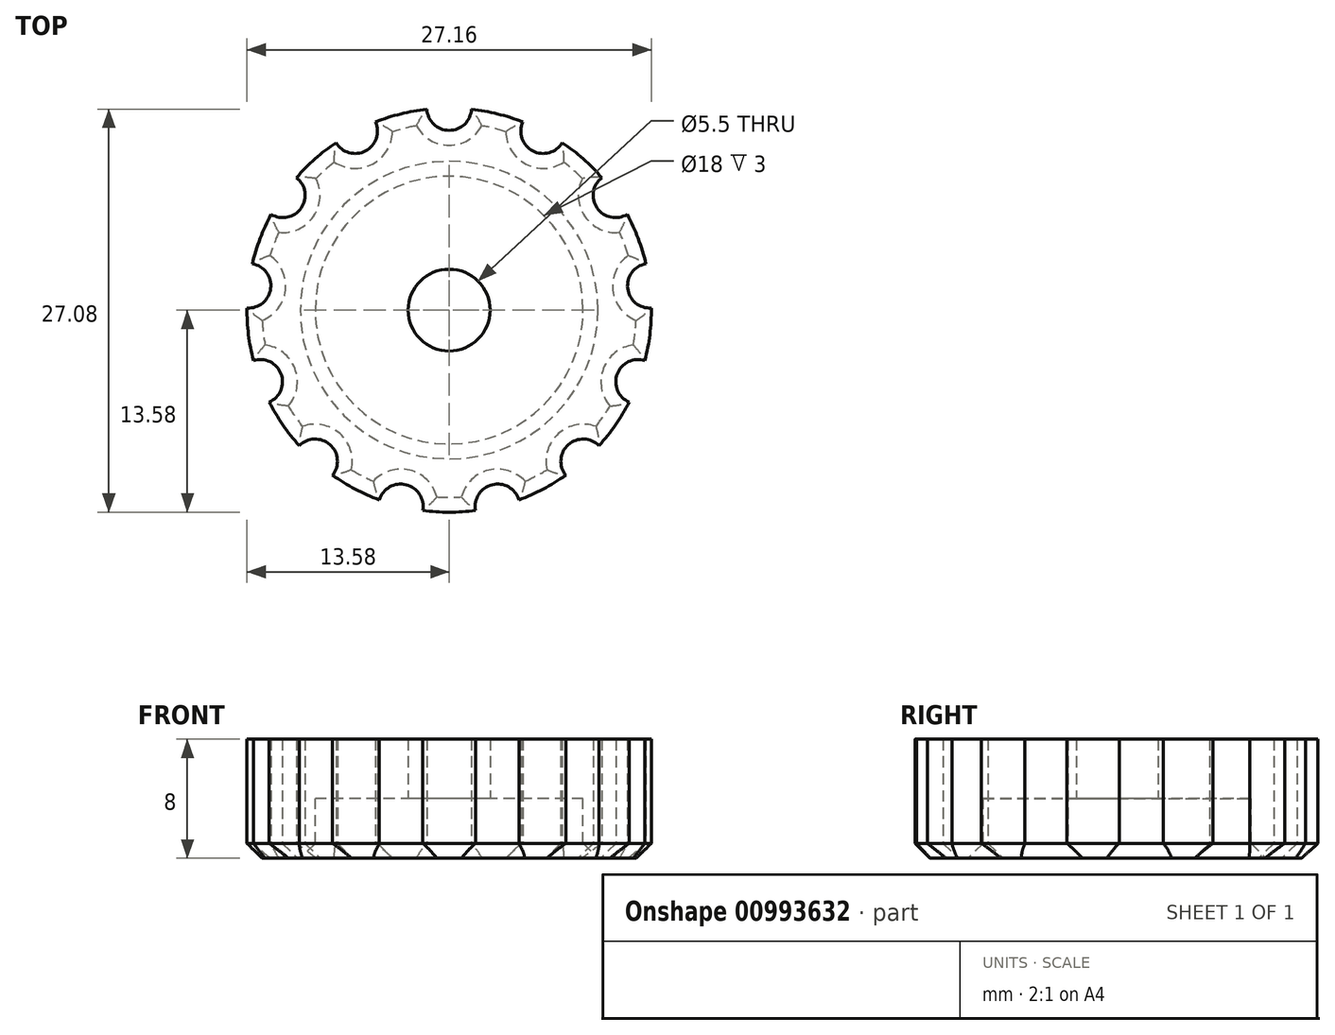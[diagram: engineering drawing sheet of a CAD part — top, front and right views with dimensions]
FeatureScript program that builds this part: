
annotation { "Feature Type Name" : "Feature", "Feature Type Description" : "" }
export const myFeature = defineFeature(function(context is Context, id is Id, definition is map)
    precondition{}
    {
        {
            var Q0;
            Q0=qCreatedBy(makeId("Top.planeOp"),FACE);
            var sketch = newSketch(context, id + "F0", { "sketchPlane" : qUnion([Q0])});
            skCircle(sketch, "E0", {"center": v(0, 0) * mm, "radius": 2.75 * mm});
            skCircle(sketch, "E1", {"center": v(0, 0) * mm, "radius": 13.58 * mm});
            skCircle(sketch, "E2", {"center": v(0, 13.58) * mm, "radius": 1.5 * mm});
            skCircle(sketch, "E3.1.0", {"center": v(-6.31, 12.02) * mm, "radius": 1.5 * mm});
            skCircle(sketch, "E3.2.0", {"center": v(-11.18, 7.71) * mm, "radius": 1.5 * mm});
            skCircle(sketch, "E3.3.0", {"center": v(-13.48, 1.64) * mm, "radius": 1.5 * mm});
            skCircle(sketch, "E3.4.0", {"center": v(-12.7, -4.82) * mm, "radius": 1.5 * mm});
            skCircle(sketch, "E3.5.0", {"center": v(-9, -10.16) * mm, "radius": 1.5 * mm});
            skPoint(sketch, "E4", {"position": v(1.5, 13.5) * mm});
            skPoint(sketch, "E5", {"position": v(4.95, 12.65) * mm});
            skCircle(sketch, "E6.1.6.0", {"center": v(-3.25, -13.19) * mm, "radius": 1.5 * mm});
            skCircle(sketch, "E7", {"center": v(0, 0) * mm, "radius": 9 * mm});
            skCircle(sketch, "E8.1.7.0", {"center": v(3.25, -13.19) * mm, "radius": 1.5 * mm});
            skCircle(sketch, "E8.1.8.0", {"center": v(9, -10.16) * mm, "radius": 1.5 * mm});
            skCircle(sketch, "E8.1.9.0", {"center": v(12.7, -4.82) * mm, "radius": 1.5 * mm});
            skCircle(sketch, "E8.1.10.0", {"center": v(13.48, 1.64) * mm, "radius": 1.5 * mm});
            skCircle(sketch, "E8.1.11.0", {"center": v(11.18, 7.71) * mm, "radius": 1.5 * mm});
            skCircle(sketch, "E8.1.12.0", {"center": v(6.31, 12.02) * mm, "radius": 1.5 * mm});
            skSolve(sketch);
        }
        {
            var Q0;
            Q0=makeQuery(id+"F0.imprint","IMPRINT",FACE,{"disambiguationData":[TD([[makeQuery(id+"F0.imprint","IMPRINT",EDGE,{"derivedFrom":sQuery(id+"F0.wireOp",EDGE,"E7")}),-1.0]])]});
            var Q1;
            Q1=makeQuery(id+"F0.imprint","IMPRINT",FACE,{"disambiguationData":[TD([[makeQuery(id+"F0.imprint","IMPRINT",EDGE,{"derivedFrom":sQuery(id+"F0.wireOp",EDGE,"E0")}),-1.0]])]});
            extrude(context, id + "F1", {"entities" : qUnion([Q0, Q1]), "depth" : 4 * mm, "offsetDistance" : 25 * mm});
        }
        {
            var Q0;
            Q0=makeQuery(id+"F0.imprint","IMPRINT",FACE,{"disambiguationData":[TD([[makeQuery(id+"F0.imprint","IMPRINT",EDGE,{"derivedFrom":sQuery(id+"F0.wireOp",EDGE,"E7")}),-1.0]])]});
            extrude(context, id + "F2", {"entities" : qUnion([Q0]), "operationType" : NewBodyOperationType.ADD, "oppositeDirection" : true, "depth" : 4 * mm, "offsetDistance" : 25 * mm});
        }
        {
            var Q0;
            Q0=makeQuery(id+"F2.opExtrude","CAP_FACE",FACE,{"disambiguationData":[OSD([sQuery(id+"F0.wireOp",EDGE,"E1"),sQuery(id+"F0.wireOp",EDGE,"E2"),sQuery(id+"F0.wireOp",EDGE,"E3.1.0"),sQuery(id+"F0.wireOp",EDGE,"E3.2.0"),sQuery(id+"F0.wireOp",EDGE,"E3.3.0"),sQuery(id+"F0.wireOp",EDGE,"E3.4.0"),sQuery(id+"F0.wireOp",EDGE,"E3.5.0"),sQuery(id+"F0.wireOp",EDGE,"E6.1.6.0"),sQuery(id+"F0.wireOp",EDGE,"E7"),sQuery(id+"F0.wireOp",EDGE,"E8.1.7.0"),sQuery(id+"F0.wireOp",EDGE,"E8.1.8.0"),sQuery(id+"F0.wireOp",EDGE,"E8.1.9.0"),sQuery(id+"F0.wireOp",EDGE,"E8.1.10.0"),sQuery(id+"F0.wireOp",EDGE,"E8.1.11.0"),sQuery(id+"F0.wireOp",EDGE,"E8.1.12.0")])],"isStart":false});
            chamfer(context, id + "F3", {"entities" : qUnion([Q0]), "width" : 1 * mm, "tangentPropagation" : true});
        }
    });
